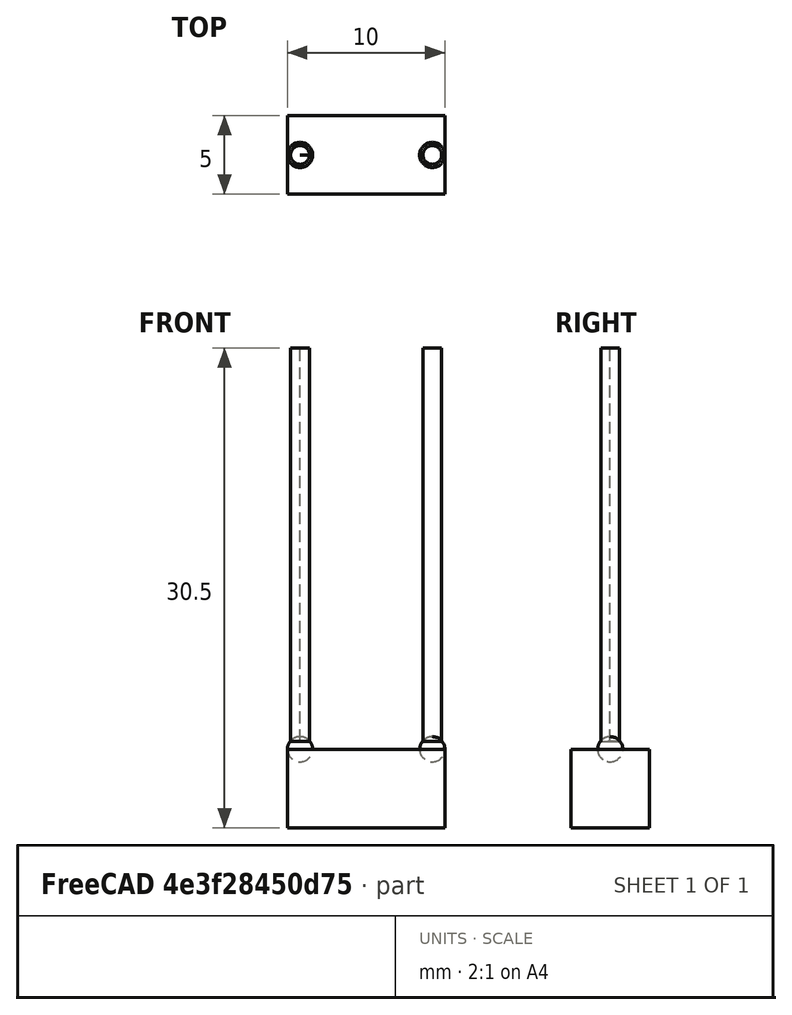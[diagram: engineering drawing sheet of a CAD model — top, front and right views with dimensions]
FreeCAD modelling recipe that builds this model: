
FCSTD DOCUMENT  (FreeCAD 1.0R39319 (Git))
Label: Сondesator(K71 – 6)
License: All rights reserved
LicenseURL: https://en.wikipedia.org/wiki/All_rights_reserved
objects: PartDesign::Body×4, PartDesign::AdditiveSphere×2, PartDesign::AdditiveCylinder×2, PartDesign::AdditiveBox×1
note: 19 computed .brp shape members not serialized (recipe doc carries the construction recipe); baked Part::Feature solids carry a one-line shape summary decoded from their .brp

FEATURE [PartDesign::AdditiveBox] Box
  AttacherType = Attacher::AttachEngine3D
  Height = 5
  Length = 10
  Refine = true
  Suppressed = false
  Width = 5
FEATURE [PartDesign::Body] Body  label="Тіло"
  AllowCompound = false
  Group = -> [Box]
  Origin = -> Origin
  Tip = -> Box
FEATURE [PartDesign::AdditiveSphere] Sphere
  Angle1 = -90
  Angle2 = 90
  Angle3 = 360
  AttacherType = Attacher::AttachEngine3D
  AttachmentOffset = pos=(0.8,2.5,0) rot=(0,0,1;0rad)
  AttachmentSupport = -> [Box]
  MapMode = 5
  Placement = pos=(0.8,2.5,5) rot=(0,0,1;0rad)
  Radius = 0.8
  Refine = true
  Suppressed = false
FEATURE [PartDesign::AdditiveSphere] Sphere001
  Angle1 = -90
  Angle2 = 90
  Angle3 = 360
  AttacherType = Attacher::AttachEngine3D
  AttachmentOffset = pos=(9.2,2.5,0) rot=(0,0,1;0rad)
  AttachmentSupport = -> [Box]
  BaseFeature = -> Sphere
  MapMode = 5
  Placement = pos=(9.2,2.5,5) rot=(0,0,1;0rad)
  Radius = 0.8
  Refine = true
  Suppressed = false
FEATURE [PartDesign::Body] Body001  label="Тіло001"
  AllowCompound = false
  Group = -> [Sphere,Sphere001]
  Origin = -> Origin001
  Tip = -> Sphere001
FEATURE [PartDesign::Body] Body002  label="Тіло002"
  AllowCompound = false
  Origin = -> Origin002
FEATURE [PartDesign::AdditiveCylinder] Cylinder
  Angle = 360
  AttacherType = Attacher::AttachEngine3D
  AttachmentOffset = pos=(0,0,0.5) rot=(0,0,1;0rad)
  AttachmentSupport = -> [Sphere001]
  FirstAngle = 0
  Height = 25
  MapMode = 2
  Placement = pos=(9.2,2.5,5.5) rot=(0,0,1;0rad)
  Radius = 0.6
  Refine = true
  SecondAngle = 0
  Suppressed = false
FEATURE [PartDesign::AdditiveCylinder] Cylinder001
  Angle = 358
  AttacherType = Attacher::AttachEngine3D
  AttachmentOffset = pos=(-8.4,0,0.5) rot=(0,0,1;0rad)
  AttachmentSupport = -> [Sphere001]
  BaseFeature = -> Cylinder
  FirstAngle = 0
  Height = 25
  MapMode = 2
  Placement = pos=(0.8,2.5,5.5) rot=(0,0,1;0rad)
  Radius = 0.6
  Refine = true
  SecondAngle = 0
  Suppressed = false
FEATURE [PartDesign::Body] Body003  label="Тіло003"
  AllowCompound = false
  Group = -> [Cylinder,Cylinder001]
  Origin = -> Origin003
  Tip = -> Cylinder001
